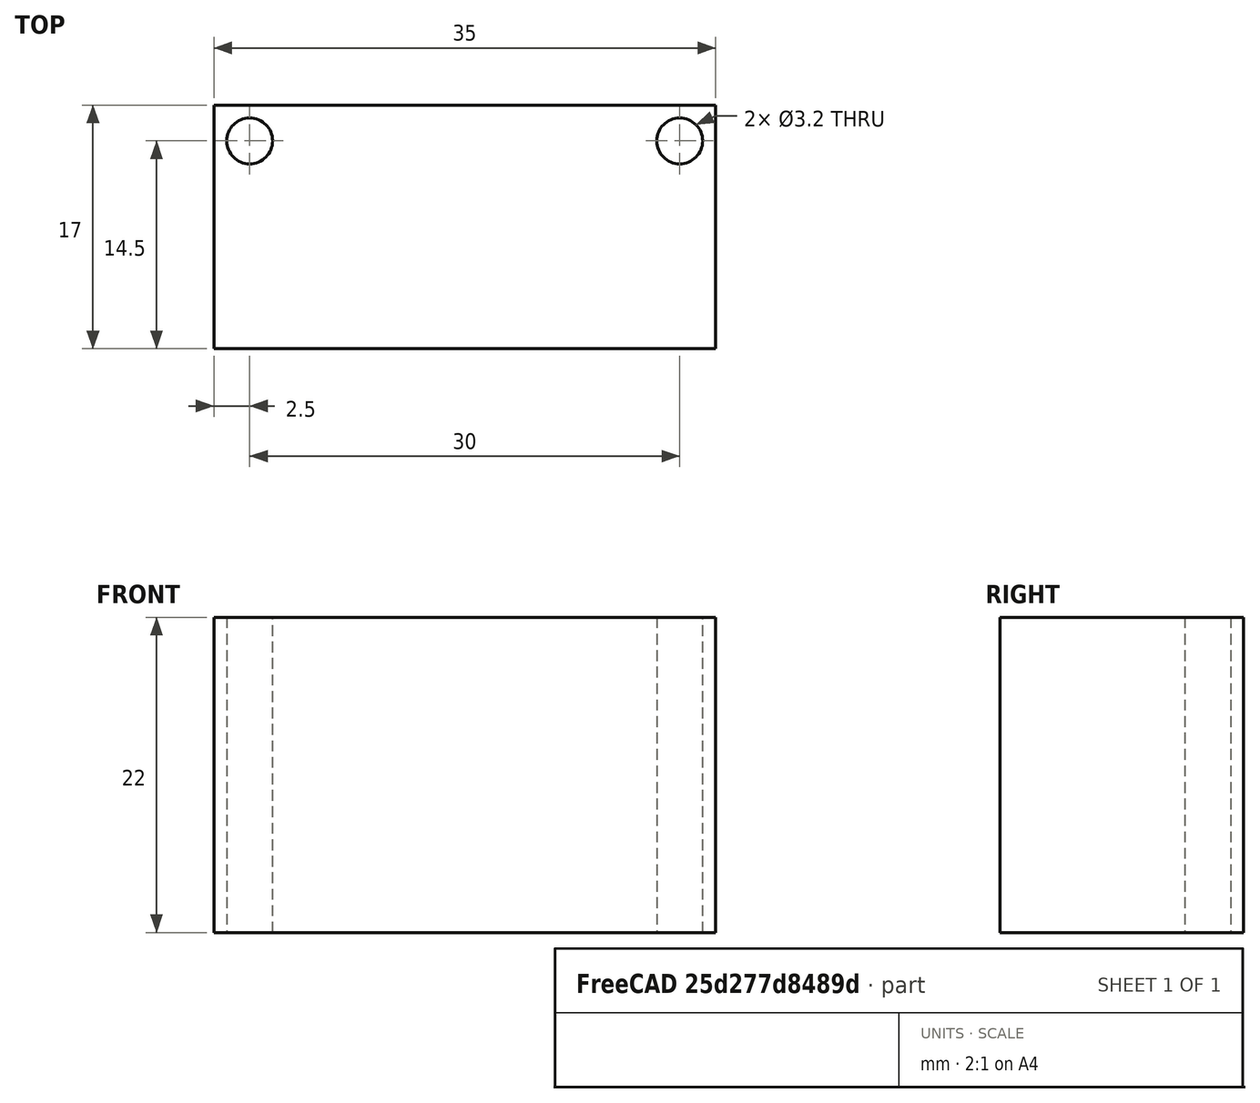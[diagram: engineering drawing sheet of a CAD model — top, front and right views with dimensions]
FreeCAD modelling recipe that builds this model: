
FCSTD DOCUMENT  (FreeCAD 0.18R16131 (Git))
Label: VoltageConverter
License: All rights reserved
LicenseURL: http://en.wikipedia.org/wiki/All_rights_reserved
objects: Sketcher::SketchObject×1, PartDesign::Pad×1, PartDesign::Body×1, App::Part×1
note: 4 computed .brp shape members not serialized (recipe doc carries the construction recipe); baked Part::Feature solids carry a one-line shape summary decoded from their .brp

FEATURE [Sketcher::SketchObject] Sketch
  MapMode = 5
  Support = -> [XY_Plane001]
  sketch-geometry (7):
    g0: LineSegment StartX=0 StartY=0 StartZ=0 EndX=35 EndY=0 EndZ=0
    g1: LineSegment StartX=35 StartY=0 StartZ=0 EndX=35 EndY=17 EndZ=0
    g2: LineSegment StartX=35 StartY=17 StartZ=0 EndX=0 EndY=17 EndZ=0
    g3: LineSegment StartX=0 StartY=17 StartZ=0 EndX=0 EndY=0 EndZ=0
    g4: Circle CenterX=2.5 CenterY=14.5 CenterZ=0 NormalX=0 NormalY=0 NormalZ=1 AngleXU=0 Radius=1.6
    g5: Circle CenterX=32.5 CenterY=14.5 CenterZ=0 NormalX=0 NormalY=0 NormalZ=1 AngleXU=0 Radius=1.6
    g6: LineSegment [constr] StartX=2.5 StartY=14.5 StartZ=0 EndX=32.5 EndY=14.5 EndZ=0
  constraints (19):
    c: Coincident(g0,g1)
    c: Coincident(g1,g2)
    c: Coincident(g2,g3)
    c: Coincident(g3,g0)
    c: Horizontal(g0)
    c: Horizontal(g2)
    c: Vertical(g1)
    c: Vertical(g3)
    c: Coincident(g0,g-1)
    c: Distance(g3) = 17
    c: Distance(g2) = 35
    c: Coincident(g6,g4)
    c: Coincident(g6,g5)
    c: Horizontal(g6)
    c: Distance(g6) = 30
    c: Equal(g4,g5)
    c: Radius(g4) = 1.6
    c: Distance(g4,g2) = 2.5
    c: Distance(g4,g3) = 2.5
FEATURE [PartDesign::Pad] Pad
  Length = 22
  Length2 = 100
  Profile = -> Sketch
  Type = 0
FEATURE [PartDesign::Body] Body
  Group = -> [Sketch,Pad]
  Origin = -> Origin001
  Tip = -> Pad
FEATURE [App::Part] Part
  Group = -> [Body]
  Origin = -> Origin
